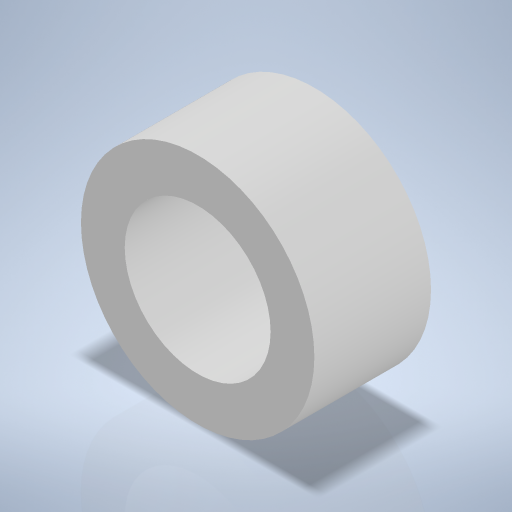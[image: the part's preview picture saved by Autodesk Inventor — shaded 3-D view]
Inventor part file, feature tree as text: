
AUTODESK INVENTOR PART (.ipt)
format: ipt  version: 2024 (Build 280153000, 153)  size: 241,152 bytes
history: native  units: mm
features: extrude x1, sketch x1
ambient origin geometry x8: Origin, YZ Plane, XZ Plane, XY Plane, X Axis, Y Axis, Z Axis, Center Point
bodies: Volumenkörper1 (feature_tree)
feature tree (2):
  extrude  "Extrusion1"  Depth=4.0mm
  sketch  "Skizze1"  dims[d0=8.0mm d2=5.0mm d3=4.0mm d4=0.0mm]
